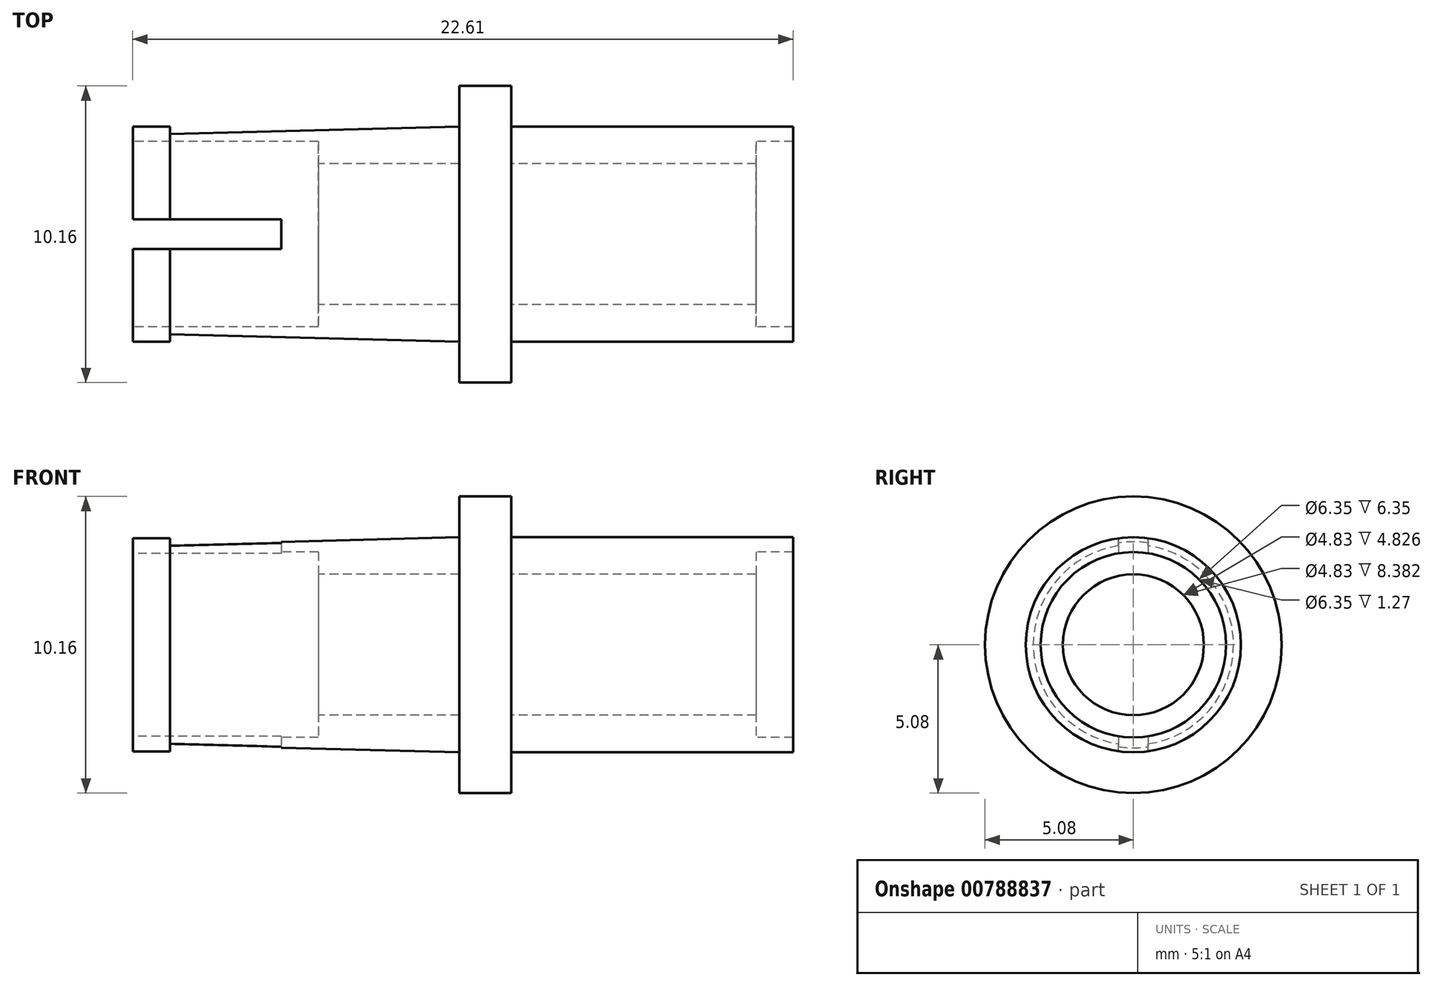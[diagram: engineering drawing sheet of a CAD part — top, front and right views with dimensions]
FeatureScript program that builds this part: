
annotation { "Feature Type Name" : "Feature", "Feature Type Description" : "" }
export const myFeature = defineFeature(function(context is Context, id is Id, definition is map)
    precondition{}
    {
        {
            var Q0;
            Q0=qCreatedBy(makeId("Front.planeOp"),FACE);
            var sketch = newSketch(context, id + "F0", { "sketchPlane" : qUnion([Q0])});
            skLineSegment(sketch, "E0", {"start": v(-10.01, 0) * mm, "end": v(12.03, 0) * mm, "construction": true});
            skLineSegment(sketch, "E1", {"start": v(0, 0) * mm, "end": v(1.78, 0) * mm});
            skLineSegment(sketch, "E2", {"start": v(1.78, 0) * mm, "end": v(1.78, 2.41) * mm});
            skLineSegment(sketch, "E3", {"start": v(1.78, 2.41) * mm, "end": v(10.16, 2.41) * mm});
            skLineSegment(sketch, "E4", {"start": v(10.16, 2.41) * mm, "end": v(10.16, 3.18) * mm});
            skLineSegment(sketch, "E5", {"start": v(10.16, 3.18) * mm, "end": v(11.43, 3.18) * mm});
            skLineSegment(sketch, "E6", {"start": v(11.43, 3.18) * mm, "end": v(11.43, 3.68) * mm});
            skLineSegment(sketch, "E7", {"start": v(11.43, 3.68) * mm, "end": v(1.78, 3.68) * mm});
            skLineSegment(sketch, "E8", {"start": v(1.78, 3.68) * mm, "end": v(1.78, 5.08) * mm});
            skLineSegment(sketch, "E9", {"start": v(1.78, 5.08) * mm, "end": v(0, 5.08) * mm});
            skLineSegment(sketch, "E10", {"start": v(0, 5.08) * mm, "end": v(0, 3.68) * mm});
            skLineSegment(sketch, "E11", {"start": v(-9.9, 3.68) * mm, "end": v(-11.18, 3.68) * mm});
            skLineSegment(sketch, "E12", {"start": v(-11.18, 3.68) * mm, "end": v(-11.18, 3.17) * mm});
            skLineSegment(sketch, "E13", {"start": v(-11.18, 3.17) * mm, "end": v(-4.83, 3.17) * mm});
            skLineSegment(sketch, "E14", {"start": v(-4.83, 3.17) * mm, "end": v(-4.83, 2.41) * mm});
            skLineSegment(sketch, "E15", {"start": v(-4.83, 2.41) * mm, "end": v(0, 2.41) * mm});
            skLineSegment(sketch, "E16", {"start": v(0, 2.41) * mm, "end": v(0, 0) * mm});
            skLineSegment(sketch, "E17", {"start": v(-9.9, 3.68) * mm, "end": v(-9.9, 3.43) * mm});
            skLineSegment(sketch, "E18", {"start": v(-9.9, 3.43) * mm, "end": v(0, 3.68) * mm});
            skSolve(sketch);
        }
        {
            var Q0;
            Q0=makeQuery(id+"F0.imprint","IMPRINT",FACE,{"disambiguationData":[TD([[makeQuery(id+"F0.imprint","IMPRINT",EDGE,{"derivedFrom":sQuery(id+"F0.wireOp",EDGE,"E1")}),1.0]])]});
            var Q1;
            Q1=sQuery(id+"F0.wireOp",EDGE,"E0");
            revolve(context, id + "F1", {"surfaceOperationType" : NewSurfaceOperationType.NEW, "entities" : qUnion([Q0]), "axis" : qUnion([Q1]), "revolveType" : RevolveType.FULL});
        }
        {
            var Q0;
            Q0=makeQuery(id+"F1.opRevolve","SWEPT_FACE",FACE,{"disambiguationData":[OSD([sQuery(id+"F0.wireOp",EDGE,"E12")])]});
            var sketch = newSketch(context, id + "F2", { "sketchPlane" : qUnion([Q0])});
            skLineSegment(sketch, "E19.bottom", {"start": v(-0.5, 5.08) * mm, "end": v(0.5, 5.08) * mm});
            skLineSegment(sketch, "E19.top", {"start": v(-0.5, -5.08) * mm, "end": v(0.5, -5.08) * mm});
            skLineSegment(sketch, "E19.left", {"start": v(-0.5, 5.08) * mm, "end": v(-0.5, -5.08) * mm});
            skLineSegment(sketch, "E19.right", {"start": v(0.5, 5.08) * mm, "end": v(0.5, -5.08) * mm});
            skPoint(sketch, "E19.middle", {"position": v(0, 0) * mm});
            skSolve(sketch);
        }
        {
            var Q0;
            {var subQ0=sQuery(id+"F2.wireOp",EDGE,"E19.left");var subQ1=sQuery(id+"F0.wireOp",EDGE,"E12");var subQ2=makeQuery(id+"F1.opRevolve","SWEPT_EDGE",EDGE,{"disambiguationData":[OSD([sQuery(id+"F0.wireOp",EDGE,"E11"),subQ1])]});var subQ3=makeQuery(id+"F2.imprint","INTERSECT",VERTEX,{"disambiguationData":[OD(0.0)],"derivedFrom":[subQ2,subQ0]});Q0=makeQuery(id+"F2.imprint","IMPRINT",FACE,{"disambiguationData":[TD([[makeQuery(id+"F2.imprint","IMPRINT",EDGE,{"disambiguationData":[TD([[subQ3,-1.0]])],"derivedFrom":subQ0}),1.0]])]});}
            var Q1;
            {var subQ0=sQuery(id+"F2.wireOp",EDGE,"E19.left");var subQ1=makeQuery(id+"F1.opRevolve","SWEPT_EDGE",EDGE,{"disambiguationData":[OSD([sQuery(id+"F0.wireOp",EDGE,"E12"),sQuery(id+"F0.wireOp",EDGE,"E13")])]});var subQ2=makeQuery(id+"F2.imprint","INTERSECT",VERTEX,{"disambiguationData":[OD(0.0)],"derivedFrom":[subQ1,subQ0]});Q1=makeQuery(id+"F2.imprint","IMPRINT",FACE,{"disambiguationData":[TD([[makeQuery(id+"F2.imprint","IMPRINT",EDGE,{"disambiguationData":[TD([[subQ2,-1.0]])],"derivedFrom":subQ0}),1.0]])]});}
            var Q2;
            {var subQ0=sQuery(id+"F2.wireOp",EDGE,"E19.left");var subQ1=sQuery(id+"F0.wireOp",EDGE,"E12");var subQ2=makeQuery(id+"F1.opRevolve","SWEPT_EDGE",EDGE,{"disambiguationData":[OSD([sQuery(id+"F0.wireOp",EDGE,"E11"),subQ1])]});var subQ3=makeQuery(id+"F2.imprint","INTERSECT",VERTEX,{"disambiguationData":[OD(1.0)],"derivedFrom":[subQ2,subQ0]});Q2=makeQuery(id+"F2.imprint","IMPRINT",FACE,{"disambiguationData":[TD([[makeQuery(id+"F2.imprint","IMPRINT",EDGE,{"disambiguationData":[TD([[subQ3,1.0]])],"derivedFrom":subQ0}),1.0]])]});}
            extrude(context, id + "F3", {"entities" : qUnion([Q0, Q1, Q2]), "operationType" : NewBodyOperationType.REMOVE, "oppositeDirection" : true, "depth" : 5.08 * mm, "offsetDistance" : 25.4 * mm});
        }
    });
